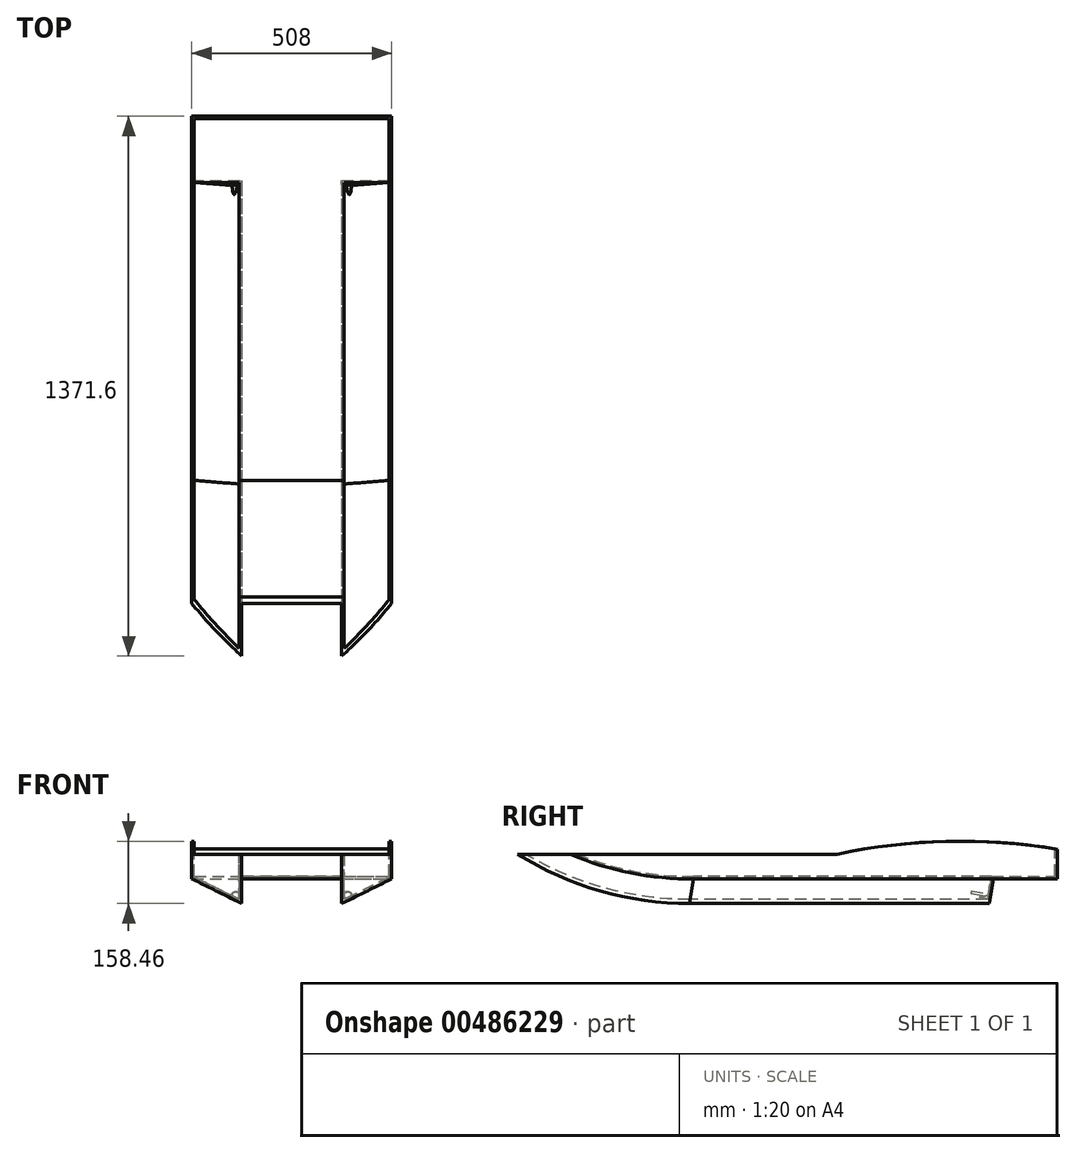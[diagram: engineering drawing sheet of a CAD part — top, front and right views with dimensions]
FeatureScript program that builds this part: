
annotation { "Feature Type Name" : "Feature", "Feature Type Description" : "" }
export const myFeature = defineFeature(function(context is Context, id is Id, definition is map)
    precondition{}
    {
        {
            var Q0;
            Q0=qCreatedBy(makeId("Right.planeOp"),FACE);
            var sketch = newSketch(context, id + "F0", { "sketchPlane" : qUnion([Q0])});
            skLineSegment(sketch, "E0", {"start": v(-525.4, 0) * mm, "end": v(693.8, 0) * mm});
            skLineSegment(sketch, "E1", {"start": v(693.8, 0) * mm, "end": v(673.28, -125.33) * mm});
            skLineSegment(sketch, "E2", {"start": v(673.28, -125.33) * mm, "end": v(-88.72, -125.33) * mm});
            skArc(sketch, "E3", {"start": v(-525.4, 0) * mm, "mid": v(-315.87, -93.38) * mm, "end": v(-88.72, -125.33) * mm});
            skSolve(sketch);
        }
        {
            var Q0;
            Q0=makeQuery(id+"F0.imprint","IMPRINT",FACE,{"disambiguationData":[TD([[makeQuery(id+"F0.imprint","IMPRINT",EDGE,{"derivedFrom":sQuery(id+"F0.wireOp",EDGE,"E0")}),-1.0]])]});
            extrude(context, id + "F1", {"entities" : qUnion([Q0]), "depth" : 508 * mm, "offsetDistance" : 25.4 * mm});
        }
        {
            var Q0;
            Q0=makeQuery(id+"F1.opExtrude","SWEPT_FACE",FACE,{"disambiguationData":[OSD([sQuery(id+"F0.wireOp",EDGE,"E1")])]});
            var sketch = newSketch(context, id + "F2", { "sketchPlane" : qUnion([Q0])});
            skLineSegment(sketch, "E4", {"start": v(-254, 112.08) * mm, "end": v(-254, -14.92) * mm, "construction": true});
            skLineSegment(sketch, "E5", {"start": v(-254, -14.92) * mm, "end": v(-254, 48.58) * mm, "construction": true});
            skLineSegment(sketch, "E6", {"start": v(-254, 48.58) * mm, "end": v(0, 48.58) * mm, "construction": true});
            skLineSegment(sketch, "E7", {"start": v(0, 48.58) * mm, "end": v(-254, 48.58) * mm, "construction": true});
            skLineSegment(sketch, "E8", {"start": v(-254, 48.58) * mm, "end": v(-508, 48.58) * mm, "construction": true});
            skLineSegment(sketch, "E9", {"start": v(-254, 48.58) * mm, "end": v(-127, 48.58) * mm, "construction": true});
            skLineSegment(sketch, "E10", {"start": v(-254, 48.58) * mm, "end": v(-381, 48.58) * mm, "construction": true});
            skLineSegment(sketch, "E11", {"start": v(-381, 48.58) * mm, "end": v(-406.4, 48.58) * mm, "construction": true});
            skLineSegment(sketch, "E12", {"start": v(-508, 48.58) * mm, "end": v(-508, -14.92) * mm});
            skLineSegment(sketch, "E13", {"start": v(-508, -14.92) * mm, "end": v(-508, -46.14) * mm});
            skLineSegment(sketch, "E14.MirrorCS", {"start": v(0, -14.92) * mm, "end": v(0, -46.14) * mm});
            skLineSegment(sketch, "E15.MirrorCS", {"start": v(0, 48.58) * mm, "end": v(0, -14.92) * mm});
            skLineSegment(sketch, "E16", {"start": v(-406.4, 48.58) * mm, "end": v(-101.6, 48.58) * mm});
            skLineSegment(sketch, "E17", {"start": v(0, 48.58) * mm, "end": v(-127, -14.92) * mm});
            skLineSegment(sketch, "E18", {"start": v(-127, -14.92) * mm, "end": v(-127, 48.58) * mm});
            skLineSegment(sketch, "E19", {"start": v(-127, -14.92) * mm, "end": v(0, -14.92) * mm});
            skLineSegment(sketch, "E20", {"start": v(0, -46.14) * mm, "end": v(-508, -46.14) * mm});
            skLineSegment(sketch, "E21", {"start": v(-127, -14.92) * mm, "end": v(-127, -46.14) * mm});
            skLineSegment(sketch, "E22.MirrorCS", {"start": v(-508, 48.58) * mm, "end": v(-381, -14.92) * mm});
            skLineSegment(sketch, "E23.MirrorCS", {"start": v(-381, -14.92) * mm, "end": v(-381, 48.58) * mm});
            skLineSegment(sketch, "E24.MirrorCS", {"start": v(-381, -14.92) * mm, "end": v(-508, -14.92) * mm});
            skLineSegment(sketch, "E25.MirrorCS", {"start": v(-381, -14.92) * mm, "end": v(-381, -46.14) * mm});
            skLineSegment(sketch, "E26", {"start": v(-381, -14.92) * mm, "end": v(-508, 48.58) * mm});
            skLineSegment(sketch, "E27", {"start": v(0, -14.92) * mm, "end": v(-127, -14.92) * mm});
            skLineSegment(sketch, "E28", {"start": v(-381, 48.58) * mm, "end": v(-508, 48.58) * mm});
            skLineSegment(sketch, "E29", {"start": v(0, 48.58) * mm, "end": v(-127, 48.58) * mm});
            skLineSegment(sketch, "E30", {"start": v(-381, -14.92) * mm, "end": v(-127, -14.92) * mm});
            skLineSegment(sketch, "E31", {"start": v(-381, 48.58) * mm, "end": v(-127, 48.58) * mm});
            skSolve(sketch);
        }
        {
            var Q0;
            Q0=makeQuery(id+"F2.imprint","IMPRINT",FACE,{"disambiguationData":[TD([[makeQuery(id+"F2.imprint","IMPRINT",EDGE,{"derivedFrom":sQuery(id+"F2.wireOp",EDGE,"E12")}),1.0]])]});
            var Q1;
            {var subQ0=sQuery(id+"F2.wireOp",EDGE,"E13");Q1=makeQuery(id+"F2.imprint","IMPRINT",FACE,{"disambiguationData":[TD([[makeQuery(id+"F2.imprint","IMPRINT",EDGE,{"derivedFrom":subQ0}),1.0]])]});}
            var Q2;
            {var subQ0=sQuery(id+"F2.wireOp",EDGE,"E21");Q2=makeQuery(id+"F2.imprint","IMPRINT",FACE,{"disambiguationData":[TD([[makeQuery(id+"F2.imprint","IMPRINT",EDGE,{"derivedFrom":subQ0}),-1.0]])]});}
            var Q3;
            {var subQ2=sQuery(id+"F2.wireOp",EDGE,"E18");Q3=makeQuery(id+"F2.imprint","IMPRINT",FACE,{"disambiguationData":[TD([[makeQuery(id+"F2.imprint","IMPRINT",EDGE,{"derivedFrom":subQ2}),1.0]])]});}
            var Q4;
            Q4=makeQuery(id+"F2.imprint","IMPRINT",FACE,{"disambiguationData":[TD([[makeQuery(id+"F2.imprint","IMPRINT",EDGE,{"derivedFrom":sQuery(id+"F2.wireOp",EDGE,"E15.MirrorCS")}),-1.0]])]});
            var Q5;
            {var subQ0=sQuery(id+"F2.wireOp",EDGE,"E14.MirrorCS");Q5=makeQuery(id+"F2.imprint","IMPRINT",FACE,{"disambiguationData":[TD([[makeQuery(id+"F2.imprint","IMPRINT",EDGE,{"derivedFrom":subQ0}),-1.0]])]});}
            var Q6;
            Q6=makeQuery(id+"F1.opExtrude","CAP_EDGE",EDGE,{"disambiguationData":[OSD([sQuery(id+"F0.wireOp",EDGE,"E2")])],"isStart":true});
            var Q7;
            Q7=makeQuery(id+"F1.opExtrude","CAP_EDGE",EDGE,{"disambiguationData":[OSD([sQuery(id+"F0.wireOp",EDGE,"E3")])],"isStart":true});
            sweep(context, id + "F3", {"operationType" : NewBodyOperationType.REMOVE, "profiles" : qUnion([Q0, Q1, Q2, Q3, Q4, Q5]), "path" : qUnion([Q6, Q7])});
        }
        {
            var Q0;
            Q0=makeQuery(id+"F1.opExtrude","CAP_FACE",FACE,{"disambiguationData":[OSD([sQuery(id+"F0.wireOp",EDGE,"E0"),sQuery(id+"F0.wireOp",EDGE,"E1"),sQuery(id+"F0.wireOp",EDGE,"E2"),sQuery(id+"F0.wireOp",EDGE,"E3")])],"isStart":false});
            var sketch = newSketch(context, id + "F4", { "sketchPlane" : qUnion([Q0])});
            skLineSegment(sketch, "E32", {"start": v(693.8, 0) * mm, "end": v(846.2, 0) * mm});
            skLineSegment(sketch, "E33", {"start": v(846.2, 0) * mm, "end": v(846.2, 25.4) * mm});
            skLineSegment(sketch, "E34", {"start": v(286.14, 0) * mm, "end": v(693.8, 0) * mm});
            skLineSegment(sketch, "E35", {"start": v(693.8, 0) * mm, "end": v(683.54, -62.67) * mm});
            skLineSegment(sketch, "E36", {"start": v(683.54, -62.67) * mm, "end": v(846.2, -62.67) * mm});
            skLineSegment(sketch, "E37", {"start": v(846.2, -62.67) * mm, "end": v(846.2, 0) * mm});
            skArc(sketch, "E38", {"start": v(846.2, 12.7) * mm, "mid": v(565.57, 32.74) * mm, "end": v(286.14, 0) * mm});
            skSolve(sketch);
        }
        {
            var Q0;
            Q0 = qSketchRegion(id + "F4", true);
            extrude(context, id + "F5", {"entities" : qUnion([Q0]), "operationType" : NewBodyOperationType.ADD, "oppositeDirection" : true, "depth" : 508 * mm, "offsetDistance" : 25.4 * mm});
        }
        {
            var Q0;
            Q0=makeQuery(id+"F5.opExtrude","SWEPT_FACE",FACE,{"disambiguationData":[OSD([sQuery(id+"F4.wireOp",EDGE,"E38")])]});
            var Q1;
            Q1=makeQuery(id+"F1.opExtrude","SWEPT_FACE",FACE,{"disambiguationData":[OSD([sQuery(id+"F0.wireOp",EDGE,"E0")])]});
            shell(context, id + "F6", {"entities" : qUnion([Q0, Q1]), "thickness" : 6.35 * mm});
        }
        {
            var Q0;
            {var subQ0=sQuery(id+"F0.wireOp",EDGE,"E2");var subQ1=sQuery(id+"F0.wireOp",EDGE,"E1");Q0=makeQuery(id+"F5.boolean.opBoolean","SPLIT",FACE,{"disambiguationData":[TD([makeQuery(id+"F3.boolean.opBoolean","COPY",FACE,{"derivedFrom":makeQuery(id+"F3.opSweep","SWEPT_FACE",FACE,{"disambiguationData":[OSD([subQ0,sQuery(id+"F2.wireOp",EDGE,"E22.MirrorCS")])]})})])],"derivedFrom":makeQuery(id+"F1.opExtrude","SWEPT_FACE",FACE,{"disambiguationData":[OSD([subQ1])]})});}
            var sketch = newSketch(context, id + "F7", { "sketchPlane" : qUnion([Q0])});
            skLineSegment(sketch, "E39", {"start": v(-381, 48.58) * mm, "end": v(-127, 48.58) * mm, "construction": true});
            skLineSegment(sketch, "E40", {"start": v(-127, 48.58) * mm, "end": v(-254, 48.58) * mm, "construction": true});
            skLineSegment(sketch, "E41", {"start": v(-254, 48.58) * mm, "end": v(-254, -25.1) * mm, "construction": true});
            skCircle(sketch, "E42", {"center": v(-396.2, 5.89) * mm, "radius": 9.53 * mm});
            skCircle(sketch, "E43.MirrorC", {"center": v(-111.8, 5.89) * mm, "radius": 9.53 * mm});
            skSolve(sketch);
        }
        {
            var Q0;
            Q0 = qSketchRegion(id + "F7", true);
            extrude(context, id + "F8", {"entities" : qUnion([Q0]), "operationType" : NewBodyOperationType.REMOVE, "oppositeDirection" : true, "depth" : 50.8 * mm, "offsetDistance" : 25.4 * mm});
        }
    });
